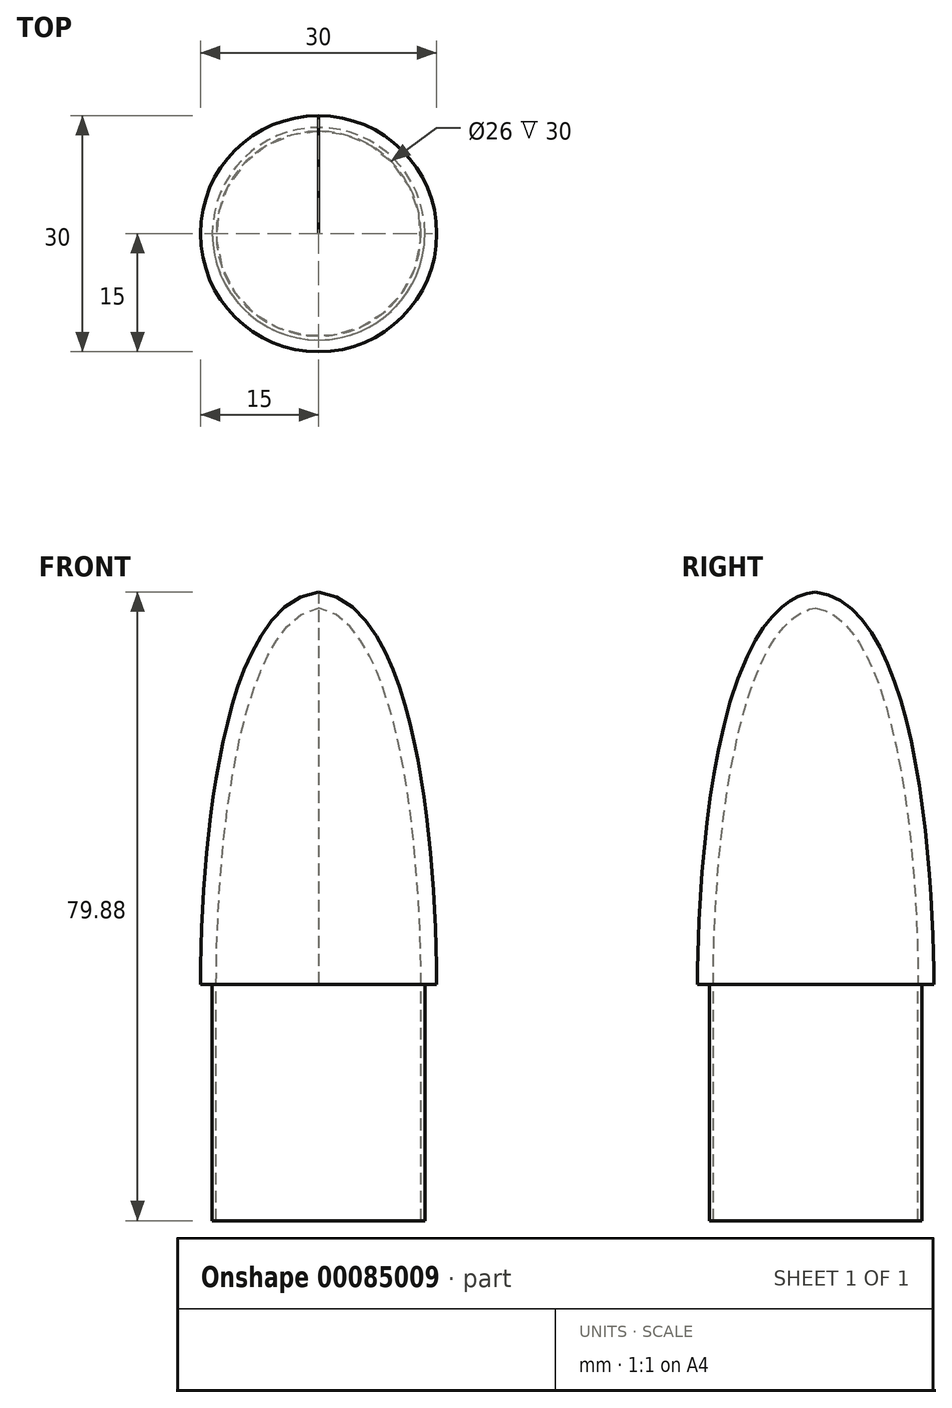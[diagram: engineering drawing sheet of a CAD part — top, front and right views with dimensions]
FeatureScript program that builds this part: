
annotation { "Feature Type Name" : "Feature", "Feature Type Description" : "" }
export const myFeature = defineFeature(function(context is Context, id is Id, definition is map)
    precondition{}
    {
        {
            var Q0;
            Q0=qCreatedBy(makeId("Right.planeOp"),FACE);
            var sketch = newSketch(context, id + "F0", { "sketchPlane" : qUnion([Q0])});
            skLineSegment(sketch, "E0.bottom", {"start": v(-15, 25) * mm, "end": v(15, 25) * mm});
            skLineSegment(sketch, "E0.top", {"start": v(-15, -25) * mm, "end": v(15, -25) * mm});
            skLineSegment(sketch, "E0.left", {"start": v(-15, 25) * mm, "end": v(-15, -25) * mm});
            skLineSegment(sketch, "E0.right", {"start": v(15, 25) * mm, "end": v(15, -25) * mm});
            skPoint(sketch, "E0.middle", {"position": v(0, 0) * mm});
            skPoint(sketch, "E1", {"position": v(0, 25) * mm});
            skFitSpline(sketch, "E2", {"points": [v(0, 25) * mm, v(-15, -25) * mm], "startDerivative": vector(-37.66, 0) * mm, "endDerivative": vector(0, -43.96) * mm});
            skFitSpline(sketch, "E3", {"points": [v(-0.96, 24.93) * mm, v(15, -25) * mm], "startDerivative": vector(42, 0.21) * mm, "endDerivative": vector(0, -41.9) * mm});
            skLineSegment(sketch, "E4", {"start": v(0, 25) * mm, "end": v(0, -25) * mm, "construction": true});
            skLineSegment(sketch, "E5", {"start": v(0, 25) * mm, "end": v(0, -25) * mm});
            skSolve(sketch);
        }
        {
            var Q0;
            {var subQ1=sQuery(id+"F0.wireOp",EDGE,"E0.top");var subQ3=sQuery(id+"F0.wireOp",EDGE,"E5");var subQ4=makeQuery(id+"F0.imprint","INTERSECT",VERTEX,{"derivedFrom":[subQ1,subQ3]});Q0=makeQuery(id+"F0.imprint","IMPRINT",FACE,{"disambiguationData":[TD([[makeQuery(id+"F0.imprint","IMPRINT",EDGE,{"disambiguationData":[TD([[subQ4,1.0]])],"derivedFrom":subQ3}),1.0]])]});}
            var Q1;
            Q1=sQuery(id+"F0.wireOp",EDGE,"E5");
            revolve(context, id + "F1", {"entities" : qUnion([Q0]), "axis" : qUnion([Q1]), "revolveType" : RevolveType.FULL});
        }
        {
            var Q0;
            Q0=makeQuery(id+"F1.opRevolve","SWEPT_FACE",FACE,{"disambiguationData":[OSD([sQuery(id+"F0.wireOp",EDGE,"E0.top")])]});
            shell(context, id + "F2", {"entities" : qUnion([Q0]), "thickness" : 2 * mm});
        }
        {
            var Q0;
            Q0=makeQuery(id+"F1.opRevolve","SWEPT_FACE",FACE,{"disambiguationData":[OSD([sQuery(id+"F0.wireOp",EDGE,"E0.top")])]});
            var sketch = newSketch(context, id + "F3", { "sketchPlane" : qUnion([Q0])});
            skCircle(sketch, "E6", {"center": v(0, 0) * mm, "radius": 13 * mm});
            skCircle(sketch, "E7", {"center": v(0, 0) * mm, "radius": 13.5 * mm});
            skSolve(sketch);
        }
        {
            var Q0;
            Q0 = qSketchRegion(id + "F3", true);
            extrude(context, id + "F4", {"entities" : qUnion([Q0]), "operationType" : NewBodyOperationType.ADD, "depth" : 30 * mm});
        }
    });
